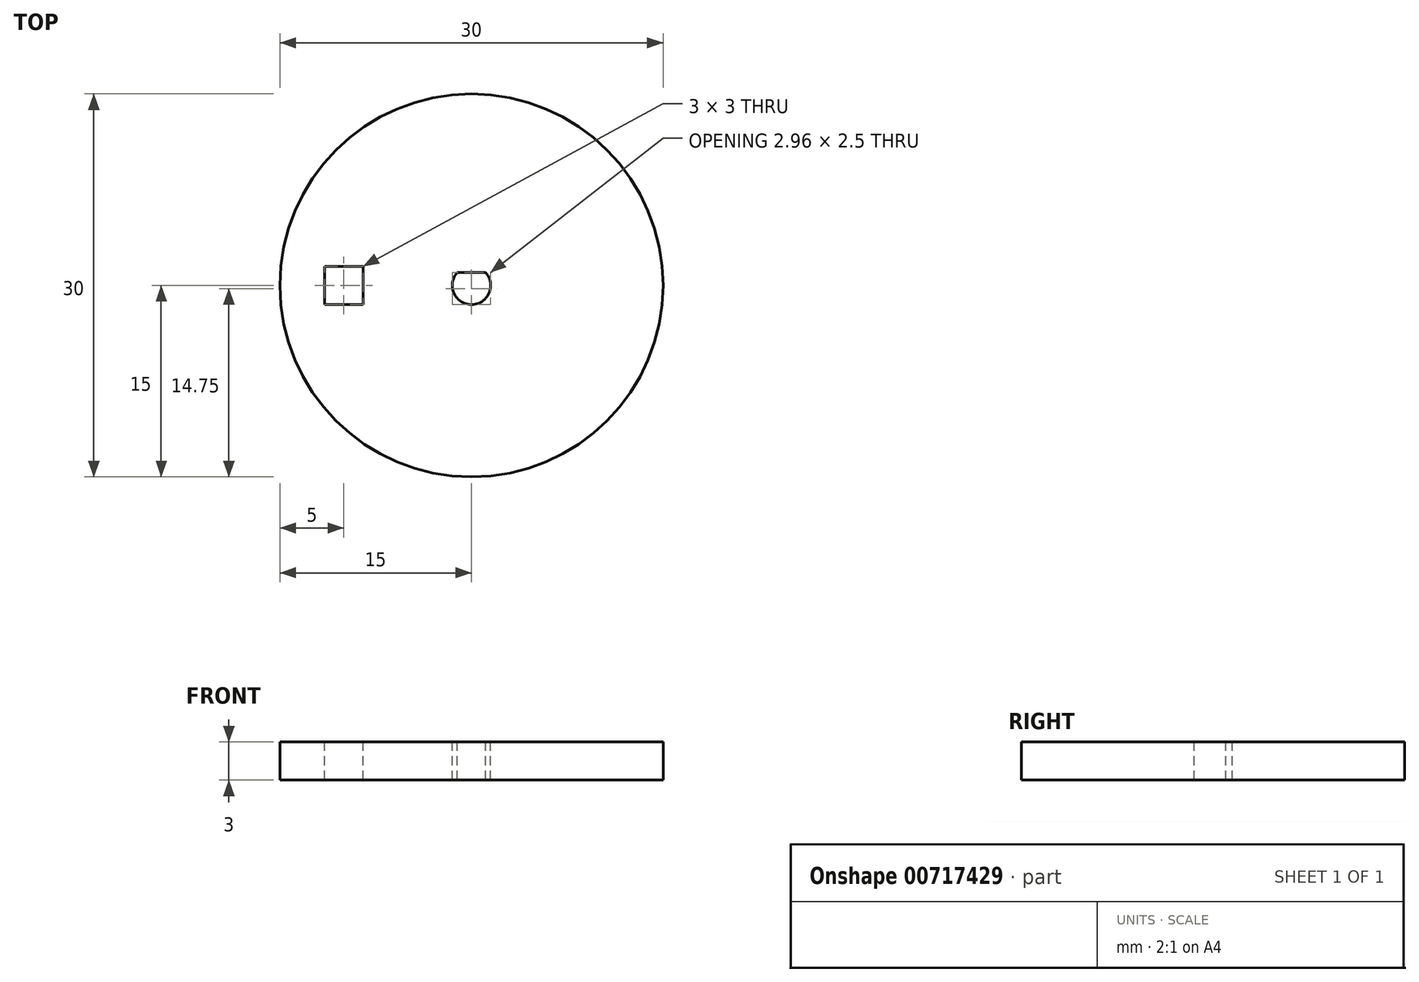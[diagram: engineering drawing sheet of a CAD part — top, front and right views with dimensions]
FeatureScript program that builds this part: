
annotation { "Feature Type Name" : "Feature", "Feature Type Description" : "" }
export const myFeature = defineFeature(function(context is Context, id is Id, definition is map)
    precondition{}
    {
        {
            assignVariable(context, id + "F0", {"name" : "Thickness", "anyValue" : 3});
        }
        {
            var Q0;
            Q0=qCreatedBy(makeId("Top.planeOp"),FACE);
            var sketch = newSketch(context, id + "F1", { "sketchPlane" : qUnion([Q0])});
            skCircle(sketch, "E0", {"center": v(0, 0) * mm, "radius": 15 * mm});
            skSolve(sketch);
        }
        {
            var Q0;
            Q0 = qSketchRegion(id + "F1", true);
            extrude(context, id + "F2", {"entities" : qUnion([Q0]), "oppositeDirection" : true, "depth" : (getVariable(context, 'Thickness')) * mm, "offsetDistance" : 25 * mm});
        }
        {
            var Q0;
            Q0=makeQuery(id+"F2.opExtrude","CAP_FACE",FACE,{"disambiguationData":[OSD([sQuery(id+"F1.wireOp",EDGE,"E0")])],"isStart":true});
            var sketch = newSketch(context, id + "F3", { "sketchPlane" : qUnion([Q0])});
            skLineSegment(sketch, "E1.bottom", {"start": v(-8.5, -1.5) * mm, "end": v(-11.5, -1.5) * mm});
            skLineSegment(sketch, "E1.top", {"start": v(-8.5, 1.5) * mm, "end": v(-11.5, 1.5) * mm});
            skLineSegment(sketch, "E1.left", {"start": v(-8.5, -1.5) * mm, "end": v(-8.5, 1.5) * mm});
            skLineSegment(sketch, "E1.right", {"start": v(-11.5, -1.5) * mm, "end": v(-11.5, 1.5) * mm});
            skPoint(sketch, "E1.middle", {"position": v(-10, 0) * mm});
            skSolve(sketch);
        }
        {
            var Q0;
            Q0 = qSketchRegion(id + "F3", true);
            extrude(context, id + "F4", {"entities" : qUnion([Q0]), "operationType" : NewBodyOperationType.REMOVE, "endBound" : BoundingType.UP_TO_NEXT, "oppositeDirection" : true, "depth" : 25 * mm, "offsetDistance" : 25 * mm});
        }
        {
            var Q0;
            Q0=makeQuery(id+"F2.opExtrude","CAP_FACE",FACE,{"disambiguationData":[OSD([sQuery(id+"F1.wireOp",EDGE,"E0")])],"isStart":true});
            var sketch = newSketch(context, id + "F5", { "sketchPlane" : qUnion([Q0])});
            skArc(sketch, "E2", {"start": v(-1.12, 1) * mm, "mid": v(0, -1.5) * mm, "end": v(1.12, 1) * mm});
            skLineSegment(sketch, "E3", {"start": v(-1.12, 1) * mm, "end": v(1.12, 1) * mm});
            skSolve(sketch);
        }
        {
            var Q0;
            Q0 = qSketchRegion(id + "F5", true);
            extrude(context, id + "F6", {"entities" : qUnion([Q0]), "operationType" : NewBodyOperationType.REMOVE, "endBound" : BoundingType.UP_TO_NEXT, "oppositeDirection" : true, "depth" : 25 * mm, "offsetDistance" : 25 * mm});
        }
    });
